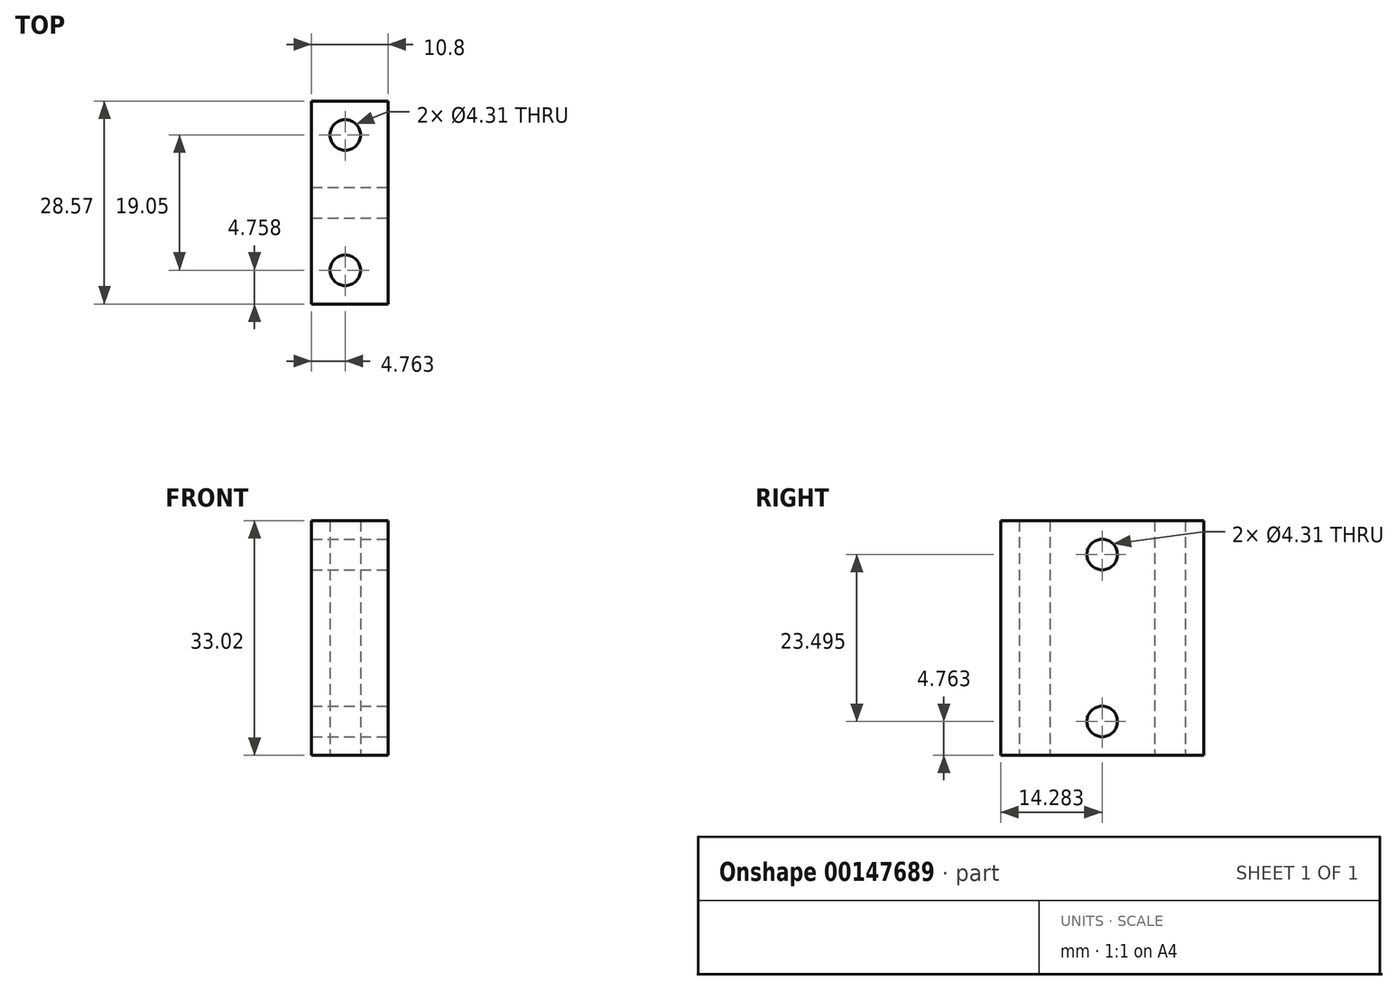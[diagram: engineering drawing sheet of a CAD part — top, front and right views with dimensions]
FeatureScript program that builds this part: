
annotation { "Feature Type Name" : "Feature", "Feature Type Description" : "" }
export const myFeature = defineFeature(function(context is Context, id is Id, definition is map)
    precondition{}
    {
        {
            var Q0;
            Q0=qCreatedBy(makeId("Top.planeOp"),FACE);
            var sketch = newSketch(context, id + "F0", { "sketchPlane" : qUnion([Q0])});
            skLineSegment(sketch, "E0.bottom", {"start": v(0, 0) * mm, "end": v(10.8, 0) * mm});
            skLineSegment(sketch, "E0.top", {"start": v(0, -28.57) * mm, "end": v(10.8, -28.57) * mm});
            skLineSegment(sketch, "E0.left", {"start": v(0, 0) * mm, "end": v(0, -28.57) * mm});
            skLineSegment(sketch, "E0.right", {"start": v(10.8, 0) * mm, "end": v(10.8, -28.57) * mm});
            skLineSegment(sketch, "E1", {"start": v(4.76, 0) * mm, "end": v(4.76, -4.76) * mm, "construction": true});
            skLineSegment(sketch, "E2", {"start": v(4.76, -4.76) * mm, "end": v(4.76, -23.81) * mm, "construction": true});
            skLineSegment(sketch, "E3", {"start": v(4.76, -23.81) * mm, "end": v(4.76, -28.57) * mm, "construction": true});
            skLineSegment(sketch, "E4", {"start": v(4.76, -4.76) * mm, "end": v(0, -4.76) * mm, "construction": true});
            skCircle(sketch, "E5", {"center": v(4.76, -4.76) * mm, "radius": 2.15 * mm});
            skCircle(sketch, "E6", {"center": v(4.76, -23.81) * mm, "radius": 2.15 * mm});
            skSolve(sketch);
        }
        {
            var Q0;
            Q0=qSketchRegion(id+"F0",true);
            extrude(context, id + "F1", {"entities" : qUnion([Q0]), "depth" : 33.02 * mm});
        }
        {
            var Q0;
            Q0=makeQuery(id+"F1.opExtrude","SWEPT_FACE",FACE,{"disambiguationData":[OSD([sQuery(id+"F0.wireOp",EDGE,"E0.right")])]});
            var sketch = newSketch(context, id + "F2", { "sketchPlane" : qUnion([Q0])});
            skCircle(sketch, "E7", {"center": v(-14.29, 4.76) * mm, "radius": 2.15 * mm});
            skLineSegment(sketch, "E8", {"start": v(-14.29, 4.76) * mm, "end": v(-14.29, 0) * mm, "construction": true});
            skLineSegment(sketch, "E9", {"start": v(-14.29, 33.02) * mm, "end": v(-14.29, 28.26) * mm, "construction": true});
            skCircle(sketch, "E10", {"center": v(-14.29, 28.26) * mm, "radius": 2.15 * mm});
            skSolve(sketch);
        }
        {
            var Q0;
            Q0=qSketchRegion(id+"F2",true);
            var Q1;
            Q1=makeQuery(id+"F1.opExtrude","SWEPT_FACE",FACE,{"disambiguationData":[OSD([sQuery(id+"F0.wireOp",EDGE,"E0.left")])]});
            extrude(context, id + "F3", {"entities" : qUnion([Q0]), "operationType" : NewBodyOperationType.REMOVE, "endBound" : BoundingType.UP_TO_SURFACE, "oppositeDirection" : true, "endBoundEntityFace" : qUnion([Q1]), "depth" : 25.4 * mm});
        }
    });
